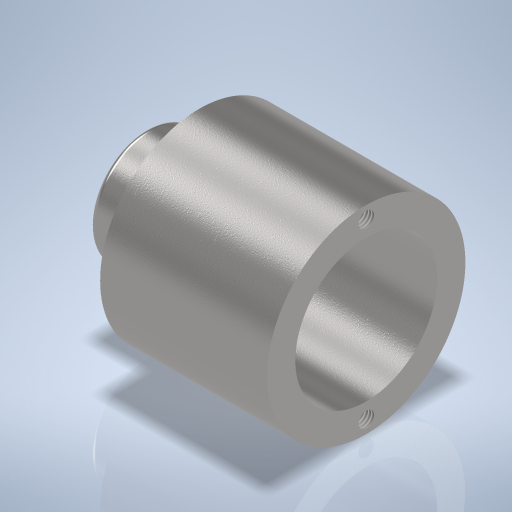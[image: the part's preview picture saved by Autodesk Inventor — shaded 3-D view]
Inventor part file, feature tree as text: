
AUTODESK INVENTOR PART (.ipt)
format: ipt  version: 2024 (Build 280153000, 153)  size: 363,520 bytes
history: native  units: mm
features: sketch x7, hole x5, revolve x1, extrude x1, fillet x1
ambient origin geometry x8: Origin, YZ Plane, XZ Plane, XY Plane, X Axis, Y Axis, Z Axis, Center Point
bodies: Volumenkörper1 (feature_tree)
feature tree (15):
  revolve  "Umdrehung1"
  extrude  "Extrusion1"  Depth=70.0mm
  hole  "Bohrung5"  [1 undecoded]
  fillet  "Rundung1"  [1 undecoded]
  hole  "Bohrung1"  [1 undecoded]
  hole  "Bohrung2"  [1 undecoded]
  hole  "Bohrung4"  [1 undecoded]
  hole  "Bohrung3"  [1 undecoded]
  sketch  "Skizze1"  dims[d0=70.0mm d1=36.0mm]
  sketch  "Skizze2"  dims[d2=17.0mm d3=63.0mm d4=90.0deg]
  sketch  "Skizze3"  dims[d5=45.0mm d6=40.0mm d7=0.0mm]
  sketch  "Skizze4"  dims[d8=20.0mm]
  sketch  "Skizze5"  dims[d9=4.0mm d10=6.0mm d11=15.0mm d12=8.5mm d13=90.0deg d14=8.0mm d15=20.594885mm]
  sketch  "Skizze6"  dims[d16=6.647mm d17=11.0mm d18=4.0mm d19=2.0mm d20=90.0deg d21=11.0mm d22=0.0mm]
  sketch  "Skizze8"  dims[d23=6.647mm d24=7.0mm d25=4.0mm d26=2.0mm d27=90.0deg d28=7.0mm d29=0.0mm d30=6.647mm d31=17.0mm d32=4.0mm d33=2.0mm d34=90.0deg d35=17.0mm d36=0.0mm d38=55.0mm d39=4.917mm d40=12.0mm d41=4.0mm d42=2.0mm d43=90.0deg d44=11.0mm d45=0.0mm d47=2.0mm]
note: 6 required parameter values undecoded (feature->parameter linkage not recoverable at this tier; creation-order binding heuristic only, values carry confidence <= 0.55)
